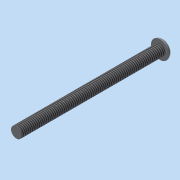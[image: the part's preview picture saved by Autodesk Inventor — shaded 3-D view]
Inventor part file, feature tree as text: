
AUTODESK INVENTOR PART (.ipt)
format: ipt  version: 2015 (Build 190159000, 159)  size: 87,552 bytes
history: native  units: mm
features: revolve x1, fillet x1, thread x1, sketch x1
ambient origin geometry x8: Origin, YZ Plane, XZ Plane, XY Plane, X Axis, Y Axis, Z Axis, Center Point
bodies: Solid1 (feature_tree)
feature tree (4):
  revolve  "Revolution1"  [1 undecoded]
  fillet  "Fillet1"  Radius=1.0mm
  thread  "Thread1"  [1 undecoded]
  sketch  "Sketch1"  dims[d0=1.5mm d1=2.5mm d2=1.0mm d3=90.0deg d4=1.0mm d5=10.0mm d6=0.0mm d7=40.0mm]
note: 2 required parameter values undecoded (feature->parameter linkage not recoverable at this tier; creation-order binding heuristic only, values carry confidence <= 0.55)